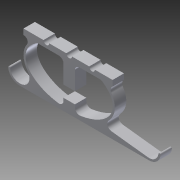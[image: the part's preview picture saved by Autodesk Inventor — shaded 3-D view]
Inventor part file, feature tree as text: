
AUTODESK INVENTOR PART (.ipt)
format: ipt  version: 2015 (Build 190159000, 159)  size: 350,208 bytes
history: native  units: mm
features: extrude x6, fillet x3, sketch x2, plane x2, pattern_linear x1, mirror x1
ambient origin geometry x8: Origin, YZ Plane, XZ Plane, XY Plane, X Axis, Y Axis, Z Axis, Center Point
bodies: Body1 (feature_tree)
feature tree (15):
  sketch  "Boceto2"  dims[d0=40.0mm d1=5.0mm]
  extrude  "Extrusión2"  Depth=5.0mm
  sketch  "Boceto4"  dims[d4=60.0mm d5=20.0mm d6=20.0mm d7=20.0mm d12=1.5mm d15=5.0mm d16=25.0mm d17=1.0mm d18=18.0mm d19=0.0mm d41=2.5mm d42=2.5mm d43=30.0mm d45=7.0mm d46=10.0mm d48=10.0mm d50=30.0mm d52=7.0mm d53=10.0mm d55=10.0mm d61=30.0mm d63=7.0mm d64=10.0mm d66=10.0mm d68=30.0mm d70=7.0mm d71=10.0mm d73=10.0mm d75=6.0mm d76=7.2mm d80=20.0mm d82=10.0mm d83=10.0mm d85=10.0mm d87=20.0mm d89=10.0mm d90=10.0mm d92=10.0mm d94=20.0mm d96=10.0mm d97=10.0mm d99=10.0mm d101=20.0mm d103=10.0mm d104=10.0mm d106=10.0mm d108=50.0mm d109=0.0mm d110=5.0mm d112=20.0mm d114=10.0mm d115=10.0mm d117=10.0mm d119=20.0mm d121=10.0mm d122=10.0mm d124=10.0mm d126=5.2mm d127=50.0mm d128=0.0mm d129=30.0mm d131=10.0mm d132=60.0mm d136=20.0mm d137=19.5mm d138=5.0mm d139=0.0mm d142=19.1mm d154=2.0mm d172=1.0mm d173=0.2mm d174=5.0mm d175=5.0mm d176=5.0mm d177=3.0mm d178=5.0mm d180=2.0mm d181=0.5mm d182=1.7mm d183=5.0mm d184=50.0mm d185=0.0mm d186=1.0mm d187=10.0mm d188=0.0mm d189=2.0mm d190=0.9mm d192=0.9mm d193=4.0mm]
  plane  "Plano de trabajo1"
  plane  "Plano de trabajo2"
  extrude  "Extrusión8"  Depth=20.0mm
  extrude  "Extrusión6"  Depth=20.0mm
  extrude  "Extrusión7"  Depth=20.0mm
  pattern_linear  "Patrón rectangular1"  Spacing1=1.5mm  [1 undecoded]
  mirror  "Simetría2"
  fillet  "Empalme7"  Radius=5.0mm
  fillet  "Empalme9"  Radius=25.0mm
  extrude  "Extrusión9"  Depth=4.0mm
  extrude  "Extrusión10"  Depth=4.0mm TaperAngle=0.0deg
  fillet  "Empalme10"  Radius=2.5mm
note: 1 required parameter value undecoded (feature->parameter linkage not recoverable at this tier; creation-order binding heuristic only, values carry confidence <= 0.55)
